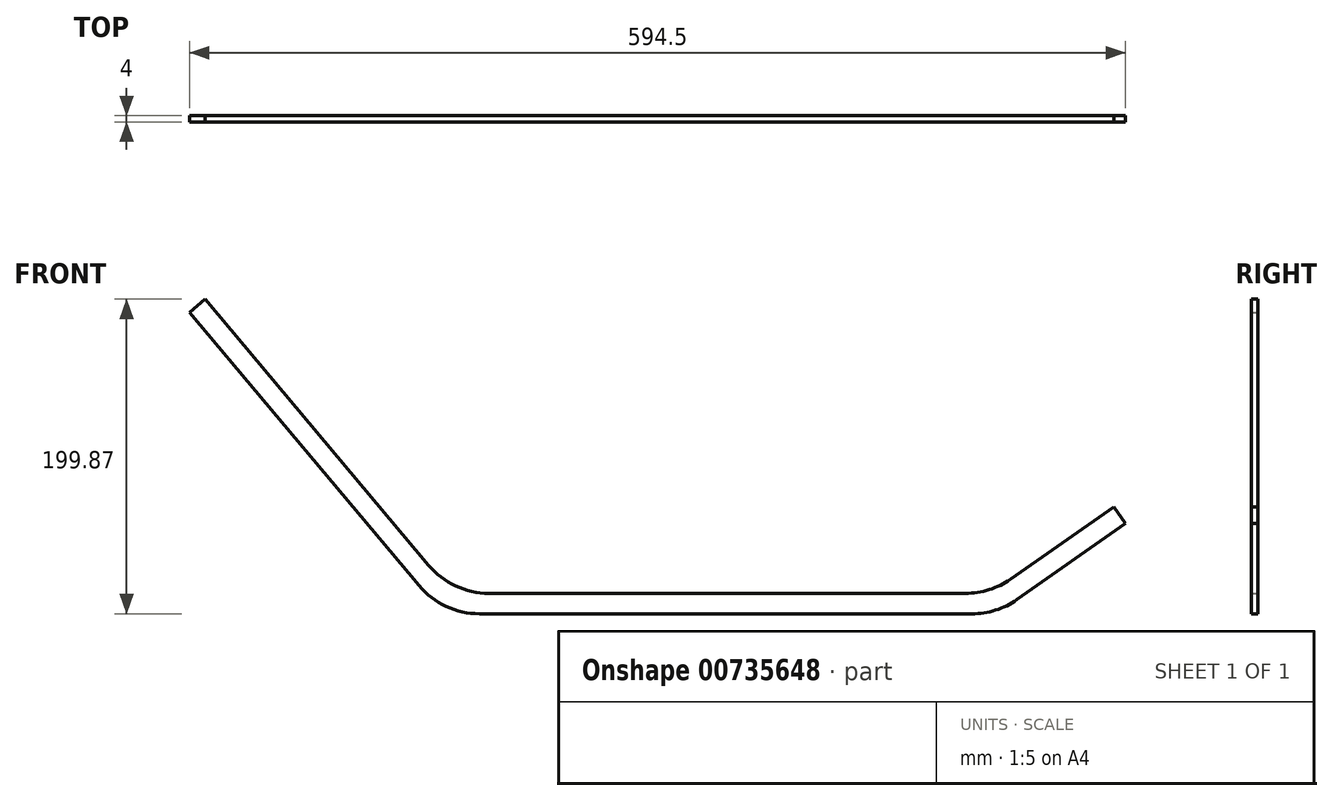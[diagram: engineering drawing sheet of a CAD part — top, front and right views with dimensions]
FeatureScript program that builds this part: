
annotation { "Feature Type Name" : "Feature", "Feature Type Description" : "" }
export const myFeature = defineFeature(function(context is Context, id is Id, definition is map)
    precondition{}
    {
        {
            var Q0;
            Q0=qCreatedBy(makeId("Front.planeOp"),FACE);
            var sketch = newSketch(context, id + "F0", { "sketchPlane" : qUnion([Q0])});
            skLineSegment(sketch, "E0.bottom", {"start": v(10.15, -12.98) * mm, "end": v(323.07, -12.98) * mm});
            skLineSegment(sketch, "E0.top", {"start": v(16.2, 0.02) * mm, "end": v(318.97, 0.02) * mm});
            skLineSegment(sketch, "E1", {"start": v(-28.16, 4.88) * mm, "end": v(-173.87, 178.53) * mm});
            skLineSegment(sketch, "E2", {"start": v(-13.17, -12.98) * mm, "end": v(-477.52, -12.98) * mm, "construction": true});
            skLineSegment(sketch, "E3", {"start": v(351.74, -3.93) * mm, "end": v(420.63, 44.3) * mm});
            skLineSegment(sketch, "E4", {"start": v(299.31, -12.98) * mm, "end": v(338.83, -12.98) * mm, "construction": true});
            skLineSegment(sketch, "E5.0", {"start": v(-22.1, 17.88) * mm, "end": v(-163.9, 186.9) * mm});
            skLineSegment(sketch, "E6.0", {"start": v(347.64, 9.07) * mm, "end": v(413.18, 54.95) * mm});
            skLineSegment(sketch, "E7", {"start": v(-173.87, 178.53) * mm, "end": v(-163.9, 186.9) * mm});
            skLineSegment(sketch, "E8", {"start": v(413.18, 54.95) * mm, "end": v(420.63, 44.3) * mm});
            skPoint(sketch, "E9.visualSharp", {"position": v(-13.17, -12.98) * mm});
            skArc(sketch, "E9.filletArc", {"start": v(-28.16, 4.88) * mm, "mid": v(-10.99, -8.3) * mm, "end": v(10.15, -12.98) * mm});
            skPoint(sketch, "E10.visualSharp", {"position": v(-7.1, 0.02) * mm});
            skArc(sketch, "E10.filletArc", {"start": v(-22.1, 17.88) * mm, "mid": v(-4.92, 4.7) * mm, "end": v(16.2, 0.02) * mm});
            skPoint(sketch, "E11.visualSharp", {"position": v(334.73, 0.02) * mm});
            skArc(sketch, "E11.filletArc", {"start": v(318.97, 0.02) * mm, "mid": v(334, 2.34) * mm, "end": v(347.64, 9.07) * mm});
            skPoint(sketch, "E12.visualSharp", {"position": v(338.83, -12.98) * mm});
            skArc(sketch, "E12.filletArc", {"start": v(323.07, -12.98) * mm, "mid": v(338.1, -10.66) * mm, "end": v(351.74, -3.93) * mm});
            skSolve(sketch);
        }
        {
            var Q0;
            Q0=qSketchRegion(id+"F0",true);
            extrude(context, id + "F1", {"entities" : qUnion([Q0]), "depth" : 4 * mm, "offsetDistance" : 25 * mm});
        }
    });
